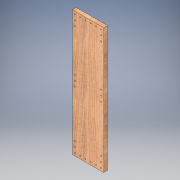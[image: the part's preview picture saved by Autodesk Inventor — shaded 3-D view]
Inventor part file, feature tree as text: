
AUTODESK INVENTOR PART (.ipt)
format: ipt  version: 2018 (Build 220112000, 112)  size: 192,000 bytes
history: native  units: in
note: dims shown in document units (in); Inventor stores cm internally (conversion verified against a paired STEP export)
features: extrude x4, sketch x4
ambient origin geometry x8: Origin, YZ Plane, XZ Plane, XY Plane, X Axis, Y Axis, Z Axis, Center Point
bodies: Solid1 (feature_tree)
feature tree (8):
  extrude  "Extrusion1"  Depth=24.0in
  extrude  "Extrusion2"  Depth=0.75in
  extrude  "Extrusion3"  Depth=0.2031in
  extrude  "Extrusion5"  Depth=0.75in
  sketch  "Sketch1"  dims[d0=6.0in d1=24.0in]
  sketch  "Sketch2"  dims[d2=0.75in d3=0.0in d4=0.5in]
  sketch  "Sketch3"  dims[d5=0.5in d6=0.2031in]
  sketch  "Sketch4"  dims[d7=0.75in d8=0.0in d9=1.0in d10=1.0in d11=1.0in d12=1.0in d13=0.75in d14=0.0in d15=11.5in d17=0.5in d19=0.2031in d22=1.0in d23=2.0in d24=0.75in d25=0.0in]
